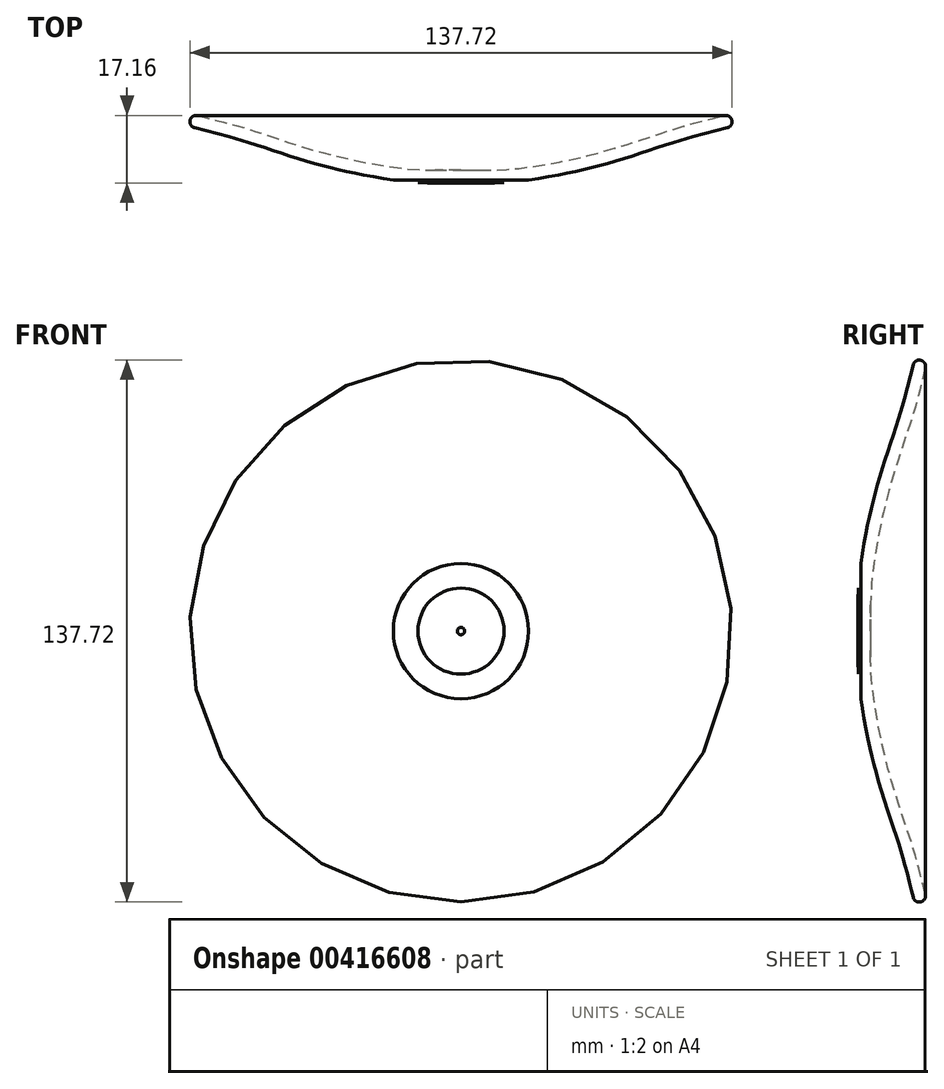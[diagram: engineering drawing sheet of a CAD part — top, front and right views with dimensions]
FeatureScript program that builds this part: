
annotation { "Feature Type Name" : "Feature", "Feature Type Description" : "" }
export const myFeature = defineFeature(function(context is Context, id is Id, definition is map)
    precondition{}
    {
        {
            var Q0;
            Q0=qCreatedBy(makeId("Top.planeOp"),FACE);
            var sketch = newSketch(context, id + "F0", { "sketchPlane" : qUnion([Q0])});
            skLineSegment(sketch, "E0", {"start": v(0, 0) * mm, "end": v(0, 3.18) * mm});
            skFitSpline(sketch, "E1", {"points": [v(0, 3.18) * mm, v(10.55, 3.18) * mm, v(34.36, 7.34) * mm, v(54.03, 13.5) * mm, v(68.43, 17.33) * mm], "startDerivative": vector(47.86, 0) * mm, "endDerivative": vector(60.36, 14.61) * mm});
            skFitSpline(sketch, "E2.0", {"points": [v(0, 0) * mm, v(0.94, 0) * mm, v(2.87, -0.05) * mm, v(6.17, -0.14) * mm, v(9.4, -0.1) * mm, v(12.34, 0.11) * mm, v(15.47, 0.42) * mm, v(19.69, 1) * mm, v(25.05, 1.93) * mm, v(29.58, 2.9) * mm, v(33.15, 3.75) * mm, v(36.65, 4.65) * mm, v(40.8, 5.86) * mm, v(45.44, 7.35) * mm, v(49.8, 8.81) * mm, v(53.24, 9.94) * mm, v(55.87, 10.75) * mm, v(58.46, 11.51) * mm, v(61.64, 12.38) * mm, v(65.41, 13.33) * mm, v(67.92, 13.94) * mm, v(69.17, 14.24) * mm]});
            skLineSegment(sketch, "E3", {"start": v(68.43, 17.33) * mm, "end": v(69.17, 14.24) * mm});
            skSolve(sketch);
        }
        {
            var Q0;
            Q0=makeQuery(id+"F0.imprint","IMPRINT",FACE,{"disambiguationData":[TD([[makeQuery(id+"F0.imprint","IMPRINT",EDGE,{"derivedFrom":sQuery(id+"F0.wireOp",EDGE,"E0")}),-1.0]])]});
            var Q1;
            Q1=sQuery(id+"F0.wireOp",EDGE,"E0");
            revolve(context, id + "F1", {"entities" : qUnion([Q0]), "axis" : qUnion([Q1]), "revolveType" : RevolveType.FULL});
        }
        {
            var Q0;
            Q0=qCreatedBy(makeId("Front.planeOp"),FACE);
            var sketch = newSketch(context, id + "F2", { "sketchPlane" : qUnion([Q0])});
            skCircle(sketch, "E4", {"center": v(0, 0) * mm, "radius": 99.82 * mm});
            skSolve(sketch);
        }
        {
            var Q0;
            Q0=makeQuery(id+"F2.imprint","IMPRINT",FACE,{"disambiguationData":[TD([[makeQuery(id+"F2.imprint","IMPRINT",EDGE,{"derivedFrom":sQuery(id+"F2.wireOp",EDGE,"E4")}),1.0]])]});
            extrude(context, id + "F3", {"entities" : qUnion([Q0]), "operationType" : NewBodyOperationType.REMOVE, "oppositeDirection" : true, "depth" : 0.64 * mm});
        }
        {
            var Q0;
            Q0=makeQuery(id+"F1.opRevolve","SWEPT_EDGE",EDGE,{"disambiguationData":[OSD([sQuery(id+"F0.wireOp",EDGE,"E1"),sQuery(id+"F0.wireOp",EDGE,"E3")])]});
            var Q1;
            Q1=makeQuery(id+"F1.opRevolve","SWEPT_EDGE",EDGE,{"disambiguationData":[OSD([sQuery(id+"F0.wireOp",EDGE,"E2.0"),sQuery(id+"F0.wireOp",EDGE,"E3")])]});
            fillet(context, id + "F4", {"entities" : qUnion([Q0, Q1]), "radius" : 1.52 * mm, "tangentPropagation" : true, "allowEdgeOverflow" : false});
        }
    });
